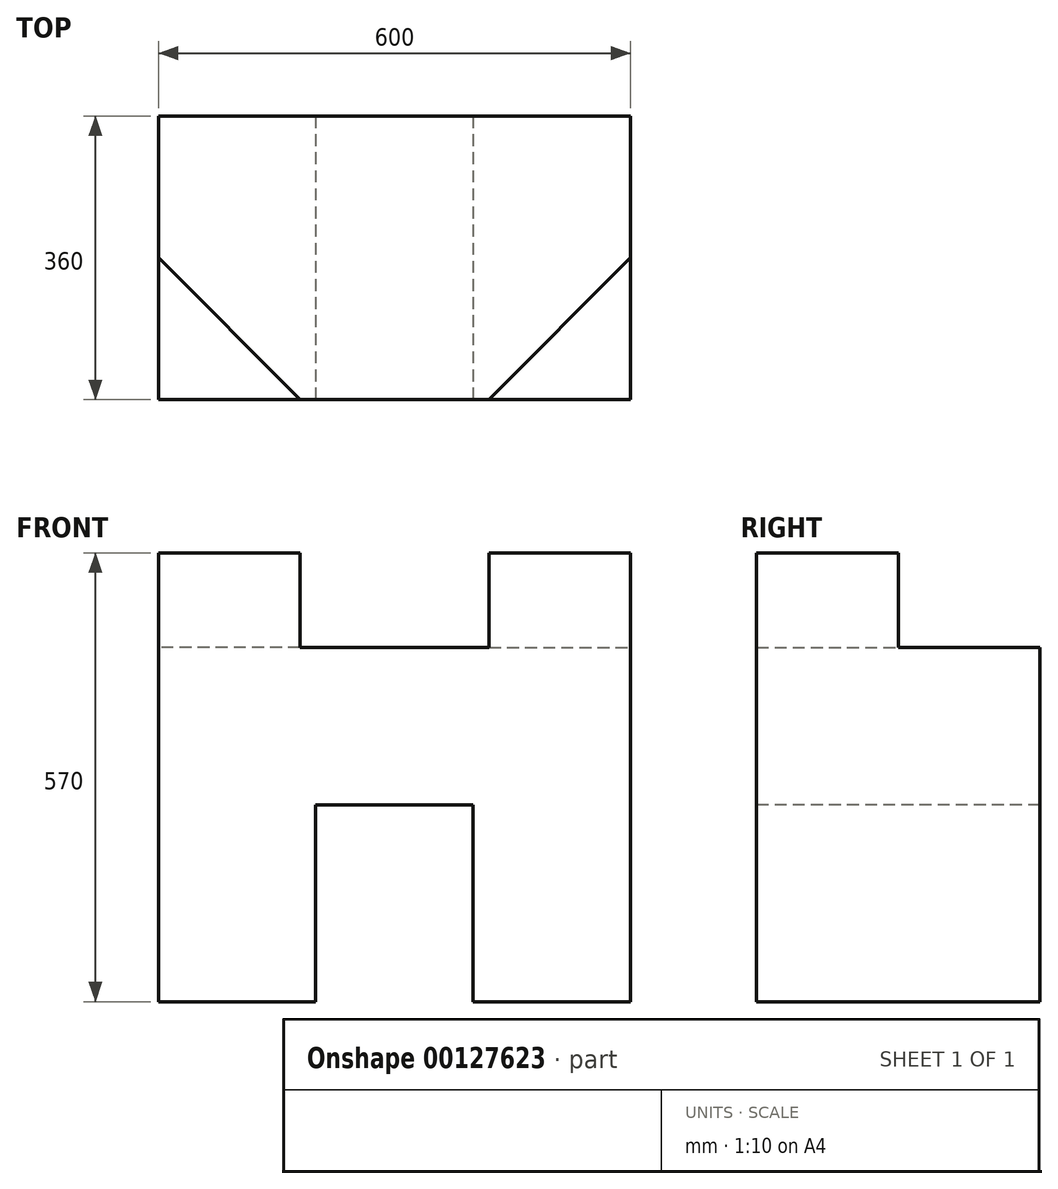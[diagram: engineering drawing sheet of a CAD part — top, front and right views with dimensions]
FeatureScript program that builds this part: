
annotation { "Feature Type Name" : "Feature", "Feature Type Description" : "" }
export const myFeature = defineFeature(function(context is Context, id is Id, definition is map)
    precondition{}
    {
        {
            var Q0;
            Q0=qCreatedBy(makeId("Top.planeOp"),FACE);
            var sketch = newSketch(context, id + "F0", { "sketchPlane" : qUnion([Q0])});
            skLineSegment(sketch, "E0.bottom", {"start": v(300, -180) * mm, "end": v(-300, -180) * mm});
            skLineSegment(sketch, "E0.top", {"start": v(300, 180) * mm, "end": v(-300, 180) * mm});
            skLineSegment(sketch, "E0.left", {"start": v(300, -180) * mm, "end": v(300, 180) * mm});
            skLineSegment(sketch, "E0.right", {"start": v(-300, -180) * mm, "end": v(-300, 180) * mm});
            skPoint(sketch, "E0.middle", {"position": v(0, 0) * mm});
            skSolve(sketch);
        }
        {
            var Q0;
            Q0 = qSketchRegion(id + "F0", true);
            var Q1;
            Q1=makeQuery(id+"F0.imprint","IMPRINT",FACE,{"disambiguationData":[TD([[makeQuery(id+"F0.imprint","IMPRINT",EDGE,{"derivedFrom":sQuery(id+"F0.wireOp",EDGE,"E0.bottom")}),-1.0]])]});
            extrude(context, id + "F1", {"entities" : qUnion([Q0, Q1]), "depth" : 450 * mm});
        }
        {
            var Q0;
            Q0=makeQuery(id+"F1.opExtrude","SWEPT_FACE",FACE,{"disambiguationData":[OSD([sQuery(id+"F0.wireOp",EDGE,"E0.bottom")])]});
            var sketch = newSketch(context, id + "F2", { "sketchPlane" : qUnion([Q0])});
            skLineSegment(sketch, "E1.bottom", {"start": v(100, 0) * mm, "end": v(-100, 0) * mm});
            skLineSegment(sketch, "E1.top", {"start": v(100, 250) * mm, "end": v(-100, 250) * mm});
            skLineSegment(sketch, "E1.left", {"start": v(100, 0) * mm, "end": v(100, 250) * mm});
            skLineSegment(sketch, "E1.right", {"start": v(-100, 0) * mm, "end": v(-100, 250) * mm});
            skPoint(sketch, "E1.middle", {"position": v(0, 125) * mm});
            skSolve(sketch);
        }
        {
            var Q0;
            Q0=makeQuery(id+"F2.imprint","IMPRINT",FACE,{"disambiguationData":[TD([[makeQuery(id+"F2.imprint","IMPRINT",EDGE,{"derivedFrom":sQuery(id+"F2.wireOp",EDGE,"E1.bottom")}),-1.0]])]});
            extrude(context, id + "F3", {"entities" : qUnion([Q0]), "operationType" : NewBodyOperationType.REMOVE, "endBound" : BoundingType.THROUGH_ALL, "oppositeDirection" : true, "depth" : 25 * mm});
        }
        {
            var Q0;
            Q0=makeQuery(id+"F1.opExtrude","CAP_FACE",FACE,{"disambiguationData":[OSD([sQuery(id+"F0.wireOp",EDGE,"E0.bottom"),sQuery(id+"F0.wireOp",EDGE,"E0.top"),sQuery(id+"F0.wireOp",EDGE,"E0.left"),sQuery(id+"F0.wireOp",EDGE,"E0.right")])],"isStart":false});
            var sketch = newSketch(context, id + "F4", { "sketchPlane" : qUnion([Q0])});
            skLineSegment(sketch, "E2", {"start": v(-300, -180) * mm, "end": v(-120, -180) * mm});
            skLineSegment(sketch, "E3", {"start": v(-120, -180) * mm, "end": v(-300, 0) * mm});
            skLineSegment(sketch, "E4", {"start": v(-300, 0) * mm, "end": v(-300, -180) * mm});
            skLineSegment(sketch, "E5", {"start": v(300, -180) * mm, "end": v(120, -180) * mm});
            skLineSegment(sketch, "E6", {"start": v(120, -180) * mm, "end": v(300, 0) * mm});
            skLineSegment(sketch, "E7", {"start": v(300, 0) * mm, "end": v(300, -180) * mm});
            skSolve(sketch);
        }
        {
            var Q0;
            Q0=makeQuery(id+"F4.imprint","IMPRINT",FACE,{"disambiguationData":[TD([[makeQuery(id+"F4.imprint","IMPRINT",EDGE,{"derivedFrom":sQuery(id+"F4.wireOp",EDGE,"E2")}),-1.0]])]});
            var Q1;
            Q1=makeQuery(id+"F4.imprint","IMPRINT",FACE,{"disambiguationData":[TD([[makeQuery(id+"F4.imprint","IMPRINT",EDGE,{"derivedFrom":sQuery(id+"F4.wireOp",EDGE,"E5")}),-1.0]])]});
            extrude(context, id + "F5", {"entities" : qUnion([Q0, Q1]), "operationType" : NewBodyOperationType.ADD, "depth" : 120 * mm});
        }
    });
